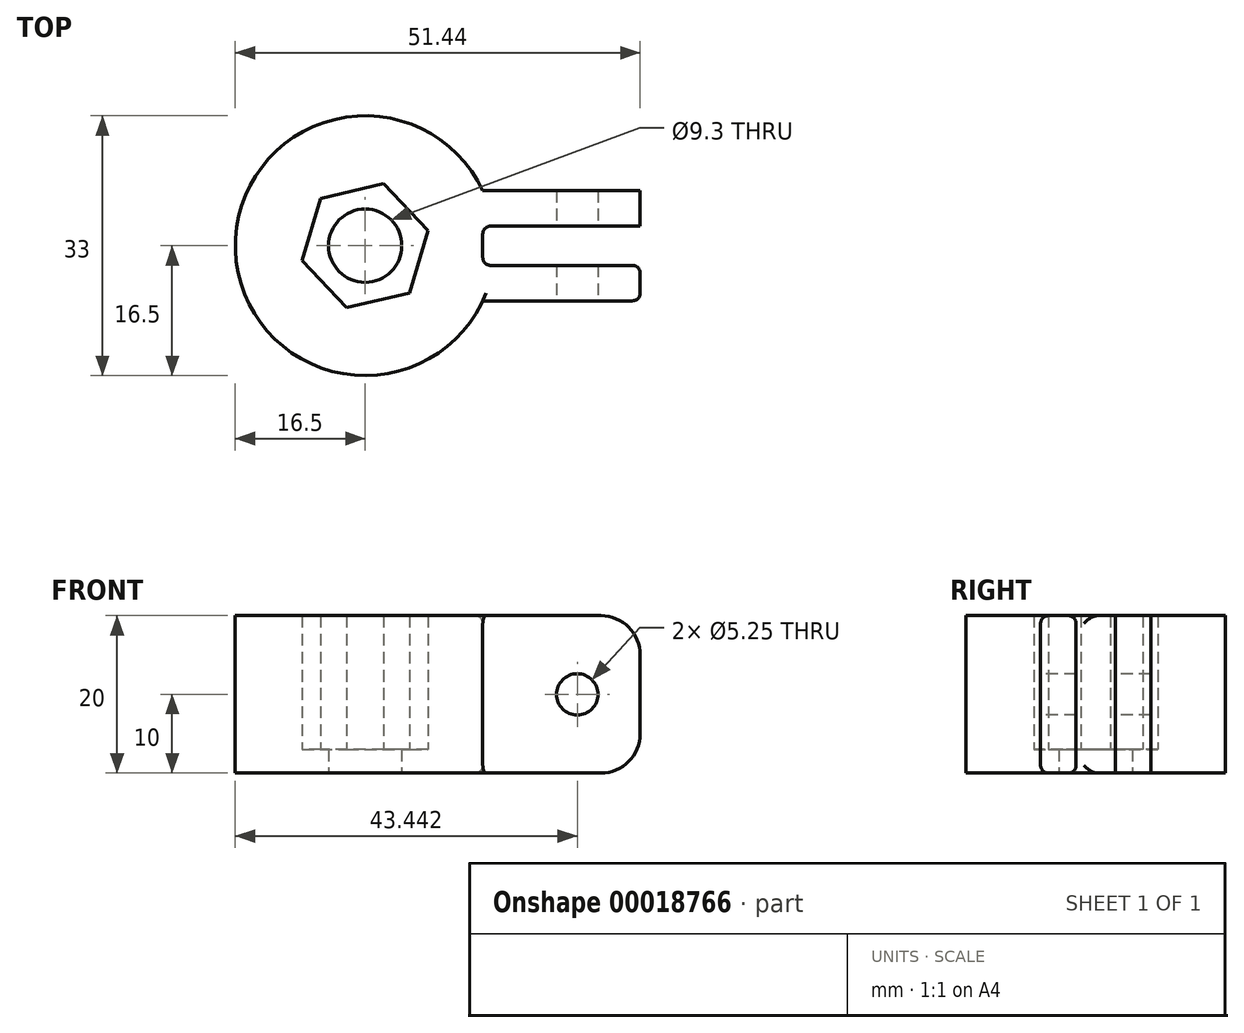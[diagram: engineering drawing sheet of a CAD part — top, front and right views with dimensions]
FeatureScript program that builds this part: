
annotation { "Feature Type Name" : "Feature", "Feature Type Description" : "" }
export const myFeature = defineFeature(function(context is Context, id is Id, definition is map)
    precondition{}
    {
        {
            var Q0;
            Q0=qCreatedBy(makeId("Top.planeOp"),FACE);
            var sketch = newSketch(context, id + "F0", { "sketchPlane" : qUnion([Q0])});
            skCircle(sketch, "E0.cCircle", {"center": v(0, 0) * mm, "radius": 7.12 * mm, "construction": true});
            skLineSegment(sketch, "E0.0", {"start": v(2.36, 7.88) * mm, "end": v(8, 1.9) * mm});
            skLineSegment(sketch, "E0.1", {"start": v(8, 1.9) * mm, "end": v(5.64, -5.99) * mm});
            skLineSegment(sketch, "E0.2", {"start": v(5.64, -5.99) * mm, "end": v(-2.36, -7.88) * mm});
            skLineSegment(sketch, "E0.3", {"start": v(-2.36, -7.88) * mm, "end": v(-8, -1.9) * mm});
            skLineSegment(sketch, "E0.4", {"start": v(-8, -1.9) * mm, "end": v(-5.64, 5.99) * mm});
            skLineSegment(sketch, "E0.5", {"start": v(-5.64, 5.99) * mm, "end": v(2.36, 7.88) * mm});
            skPoint(sketch, "E0.0.midPoint", {"position": v(5.18, 4.89) * mm});
            skCircle(sketch, "E1", {"center": v(0, 0) * mm, "radius": 16.5 * mm});
            skCircle(sketch, "E2", {"center": v(0, 0) * mm, "radius": 4.65 * mm});
            skSolve(sketch);
        }
        {
            var Q0;
            Q0=makeQuery(id+"F0.imprint","IMPRINT",FACE,{"disambiguationData":[TD([[makeQuery(id+"F0.imprint","IMPRINT",EDGE,{"derivedFrom":sQuery(id+"F0.wireOp",EDGE,"E0.0")}),1.0]])]});
            var Q1;
            Q1=makeQuery(id+"F0.imprint","IMPRINT",FACE,{"disambiguationData":[TD([[makeQuery(id+"F0.imprint","IMPRINT",EDGE,{"derivedFrom":sQuery(id+"F0.wireOp",EDGE,"E0.0")}),-1.0]])]});
            extrude(context, id + "F1", {"entities" : qUnion([Q0, Q1]), "depth" : 3 * mm});
        }
        {
            var Q0;
            Q0=makeQuery(id+"F0.imprint","IMPRINT",FACE,{"disambiguationData":[TD([[makeQuery(id+"F0.imprint","IMPRINT",EDGE,{"derivedFrom":sQuery(id+"F0.wireOp",EDGE,"E0.0")}),1.0]])]});
            extrude(context, id + "F2", {"entities" : qUnion([Q0]), "operationType" : NewBodyOperationType.ADD, "depth" : 20 * mm});
        }
        {
            var Q0;
            Q0=makeQuery(id+"F2.opExtrude","CAP_FACE",FACE,{"disambiguationData":[OSD([sQuery(id+"F0.wireOp",EDGE,"E0.0"),sQuery(id+"F0.wireOp",EDGE,"E0.1"),sQuery(id+"F0.wireOp",EDGE,"E0.2"),sQuery(id+"F0.wireOp",EDGE,"E0.3"),sQuery(id+"F0.wireOp",EDGE,"E0.4"),sQuery(id+"F0.wireOp",EDGE,"E0.5"),sQuery(id+"F0.wireOp",EDGE,"E1")])],"isStart":false});
            var sketch = newSketch(context, id + "F3", { "sketchPlane" : qUnion([Q0])});
            skLineSegment(sketch, "E3.bottom", {"start": v(14.94, 7) * mm, "end": v(34.94, 7) * mm});
            skLineSegment(sketch, "E3.top", {"start": v(14.94, -7) * mm, "end": v(34.94, -7) * mm});
            skLineSegment(sketch, "E3.left", {"start": v(14.94, 7) * mm, "end": v(14.94, -7) * mm});
            skLineSegment(sketch, "E3.right", {"start": v(34.94, 7) * mm, "end": v(34.94, -7) * mm});
            skLineSegment(sketch, "E4", {"start": v(14.94, 2.5) * mm, "end": v(34.94, 2.5) * mm});
            skLineSegment(sketch, "E5", {"start": v(34.94, 2.5) * mm, "end": v(34.94, -2.5) * mm});
            skLineSegment(sketch, "E6", {"start": v(34.94, -2.5) * mm, "end": v(14.94, -2.5) * mm});
            skSolve(sketch);
        }
        {
            var Q0;
            {var subQ0=sQuery(id+"F3.wireOp",EDGE,"E3.bottom");Q0=makeQuery(id+"F3.imprint","IMPRINT",FACE,{"disambiguationData":[TD([[makeQuery(id+"F3.imprint","IMPRINT",EDGE,{"derivedFrom":subQ0}),-1.0]])]});}
            var Q1;
            {var subQ0=sQuery(id+"F3.wireOp",EDGE,"E3.top");Q1=makeQuery(id+"F3.imprint","IMPRINT",FACE,{"disambiguationData":[TD([[makeQuery(id+"F3.imprint","IMPRINT",EDGE,{"derivedFrom":subQ0}),1.0]])]});}
            extrude(context, id + "F4", {"entities" : qUnion([Q0, Q1]), "operationType" : NewBodyOperationType.ADD, "oppositeDirection" : true, "depth" : 20 * mm});
        }
        {
            var Q0;
            {var subQ0=sQuery(id+"F3.wireOp",EDGE,"E4");var subQ1=sQuery(id+"F3.wireOp",EDGE,"E3.left");var subQ2=makeQuery(id+"F3.imprint","INTERSECT",VERTEX,{"derivedFrom":[subQ1,subQ0]});Q0=makeQuery(id+"F3.imprint","IMPRINT",FACE,{"disambiguationData":[TD([[makeQuery(id+"F3.imprint","IMPRINT",EDGE,{"disambiguationData":[TD([[subQ2,-1.0]])],"derivedFrom":subQ1}),1.0]])]});}
            extrude(context, id + "F5", {"entities" : qUnion([Q0]), "operationType" : NewBodyOperationType.REMOVE, "oppositeDirection" : true, "depth" : 25 * mm});
        }
        {
            var Q0;
            Q0=makeQuery(id+"F4.opExtrude","SWEPT_FACE",FACE,{"disambiguationData":[OSD([sQuery(id+"F3.wireOp",EDGE,"E3.top")])]});
            var sketch = newSketch(context, id + "F6", { "sketchPlane" : qUnion([Q0])});
            skCircle(sketch, "E7", {"center": v(26.94, 10) * mm, "radius": 2.62 * mm});
            skSolve(sketch);
        }
        {
            var Q0;
            Q0=makeQuery(id+"F6.imprint","IMPRINT",FACE,{"disambiguationData":[TD([[makeQuery(id+"F6.imprint","IMPRINT",EDGE,{"derivedFrom":sQuery(id+"F6.wireOp",EDGE,"E7")}),1.0]])]});
            extrude(context, id + "F7", {"entities" : qUnion([Q0]), "operationType" : NewBodyOperationType.REMOVE, "oppositeDirection" : true, "depth" : 25 * mm});
        }
        {
            var Q0;
            {var subQ0=sQuery(id+"F3.wireOp",EDGE,"E3.right");Q0=makeQuery(id+"F4.opExtrude","CAP_EDGE",EDGE,{"disambiguationData":[OSD([subQ0]),TDD([makeQuery(id+"F3.imprint","IMPRINT",EDGE,{"disambiguationData":[TD([[makeQuery(id+"F3.imprint","INTERSECT",VERTEX,{"derivedFrom":[sQuery(id+"F3.wireOp",EDGE,"E3.bottom"),subQ0]}),-1.0]])],"derivedFrom":subQ0})])],"isStart":true});}
            var Q1;
            {var subQ0=sQuery(id+"F3.wireOp",EDGE,"E3.right");Q1=makeQuery(id+"F4.opExtrude","CAP_EDGE",EDGE,{"disambiguationData":[OSD([subQ0]),TDD([makeQuery(id+"F3.imprint","IMPRINT",EDGE,{"disambiguationData":[TD([[makeQuery(id+"F3.imprint","INTERSECT",VERTEX,{"derivedFrom":[sQuery(id+"F3.wireOp",EDGE,"E3.top"),subQ0]}),1.0]])],"derivedFrom":subQ0})])],"isStart":true});}
            var Q2;
            {var subQ0=sQuery(id+"F3.wireOp",EDGE,"E3.right");Q2=makeQuery(id+"F4.opExtrude","CAP_EDGE",EDGE,{"disambiguationData":[OSD([subQ0]),TDD([makeQuery(id+"F3.imprint","IMPRINT",EDGE,{"disambiguationData":[TD([[makeQuery(id+"F3.imprint","INTERSECT",VERTEX,{"derivedFrom":[sQuery(id+"F3.wireOp",EDGE,"E3.top"),subQ0]}),1.0]])],"derivedFrom":subQ0})])],"isStart":false});}
            var Q3;
            {var subQ0=sQuery(id+"F3.wireOp",EDGE,"E3.right");Q3=makeQuery(id+"F4.opExtrude","CAP_EDGE",EDGE,{"disambiguationData":[OSD([subQ0]),TDD([makeQuery(id+"F3.imprint","IMPRINT",EDGE,{"disambiguationData":[TD([[makeQuery(id+"F3.imprint","INTERSECT",VERTEX,{"derivedFrom":[sQuery(id+"F3.wireOp",EDGE,"E3.bottom"),subQ0]}),-1.0]])],"derivedFrom":subQ0})])],"isStart":false});}
            var Q4;
            Q4=makeQuery(id+"F4.opExtrude","SWEPT_EDGE",EDGE,{"disambiguationData":[OSD([sQuery(id+"F0.wireOp",EDGE,"E1"),sQuery(id+"F3.wireOp",EDGE,"E3.top"),sQuery(id+"F3.wireOp",EDGE,"E3.left")])]});
            var Q5;
            Q5=makeQuery(id+"F4.opExtrude","SWEPT_EDGE",EDGE,{"disambiguationData":[OSD([sQuery(id+"F0.wireOp",EDGE,"E1"),sQuery(id+"F3.wireOp",EDGE,"E3.bottom"),sQuery(id+"F3.wireOp",EDGE,"E3.left")])]});
            fillet(context, id + "F8", {"entities" : qUnion([Q0, Q1, Q2, Q3, Q4, Q5]), "radius" : 5 * mm, "tangentPropagation" : true, "allowEdgeOverflow" : false});
        }
        {
            var Q0;
            Q0=makeQuery(id+"F5.boolean.opBoolean","COPY",EDGE,{"derivedFrom":makeQuery(id+"F5.opExtrude","SWEPT_EDGE",EDGE,{"disambiguationData":[OSD([sQuery(id+"F3.wireOp",EDGE,"E3.left"),sQuery(id+"F3.wireOp",EDGE,"E6")])]})});
            var Q1;
            Q1=makeQuery(id+"F5.boolean.opBoolean","COPY",EDGE,{"derivedFrom":makeQuery(id+"F5.opExtrude","SWEPT_EDGE",EDGE,{"disambiguationData":[OSD([sQuery(id+"F3.wireOp",EDGE,"E3.left"),sQuery(id+"F3.wireOp",EDGE,"E4")])]})});
            var Q2;
            Q2=makeQuery(id+"F4.opExtrude","SWEPT_EDGE",EDGE,{"disambiguationData":[OSD([sQuery(id+"F3.wireOp",EDGE,"E3.top"),sQuery(id+"F3.wireOp",EDGE,"E3.right")])]});
            var Q3;
            Q3=makeQuery(id+"F4.opExtrude","SWEPT_EDGE",EDGE,{"disambiguationData":[OSD([sQuery(id+"F3.wireOp",EDGE,"E3.right"),sQuery(id+"F3.wireOp",EDGE,"E5"),sQuery(id+"F3.wireOp",EDGE,"E6")])]});
            fillet(context, id + "F9", {"entities" : qUnion([Q0, Q1, Q2, Q3]), "radius" : 1 * mm, "tangentPropagation" : true, "allowEdgeOverflow" : false});
        }
    });
